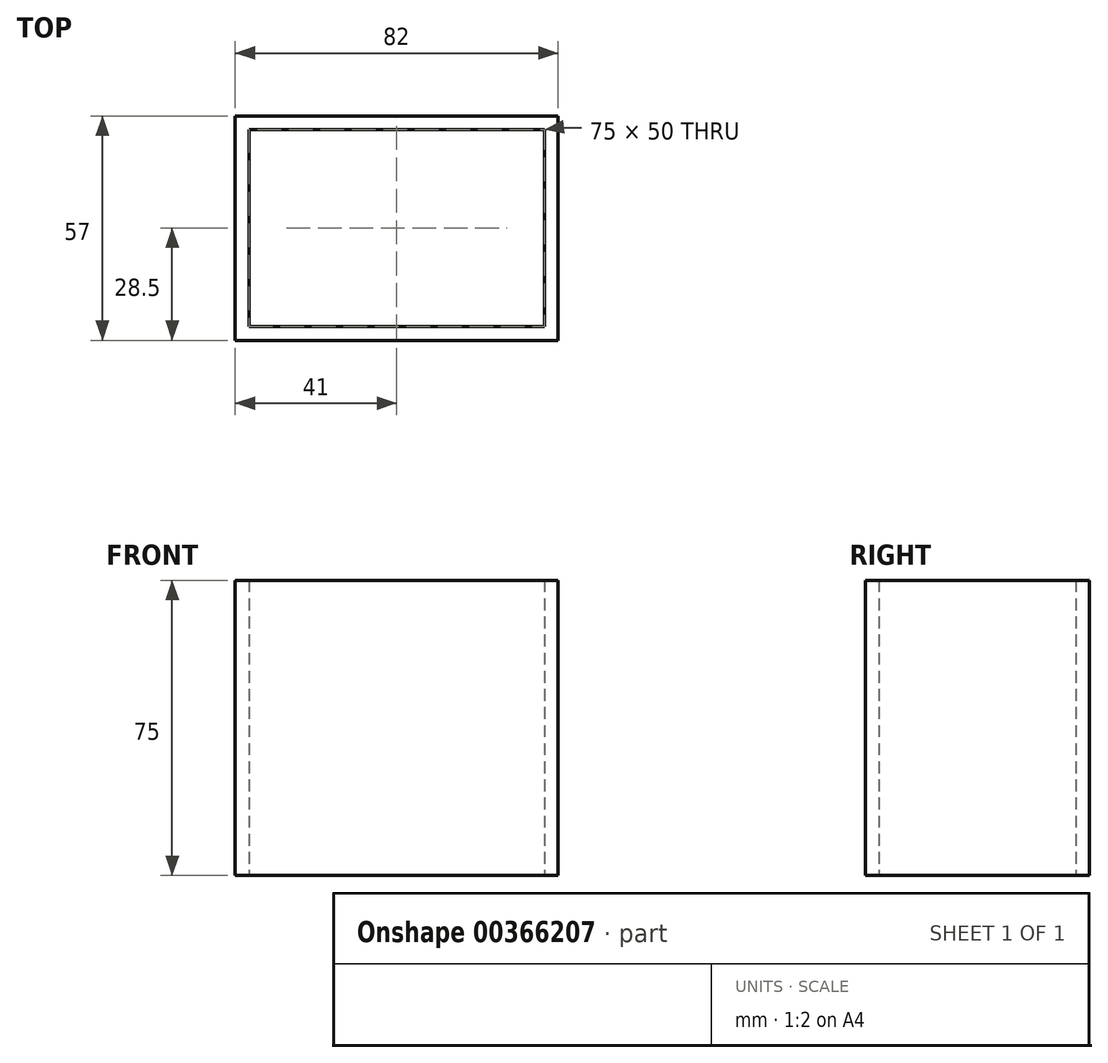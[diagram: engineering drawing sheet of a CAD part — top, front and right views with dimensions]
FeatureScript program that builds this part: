
annotation { "Feature Type Name" : "Feature", "Feature Type Description" : "" }
export const myFeature = defineFeature(function(context is Context, id is Id, definition is map)
    precondition{}
    {
        {
            var Q0;
            Q0=qCreatedBy(makeId("Top.planeOp"),FACE);
            var sketch = newSketch(context, id + "F0", { "sketchPlane" : qUnion([Q0])});
            skLineSegment(sketch, "E0.bottom", {"start": v(37.5, -25) * mm, "end": v(-37.5, -25) * mm});
            skLineSegment(sketch, "E0.top", {"start": v(37.5, 25) * mm, "end": v(-37.5, 25) * mm});
            skLineSegment(sketch, "E0.left", {"start": v(37.5, -25) * mm, "end": v(37.5, 25) * mm});
            skLineSegment(sketch, "E0.right", {"start": v(-37.5, -25) * mm, "end": v(-37.5, 25) * mm});
            skPoint(sketch, "E0.middle", {"position": v(0, 0) * mm});
            skLineSegment(sketch, "E1.bottom", {"start": v(41, -28.5) * mm, "end": v(-41, -28.5) * mm});
            skLineSegment(sketch, "E1.top", {"start": v(41, 28.5) * mm, "end": v(-41, 28.5) * mm});
            skLineSegment(sketch, "E1.left", {"start": v(41, -28.5) * mm, "end": v(41, 28.5) * mm});
            skLineSegment(sketch, "E1.right", {"start": v(-41, -28.5) * mm, "end": v(-41, 28.5) * mm});
            skSolve(sketch);
        }
        {
            var Q0;
            Q0=makeQuery(id+"F0.imprint","IMPRINT",FACE,{"disambiguationData":[TD([[makeQuery(id+"F0.imprint","IMPRINT",EDGE,{"derivedFrom":sQuery(id+"F0.wireOp",EDGE,"E0.bottom")}),1.0]])]});
            extrude(context, id + "F1", {"entities" : qUnion([Q0]), "endBound" : BoundingType.SYMMETRIC, "depth" : 75 * mm});
        }
    });
